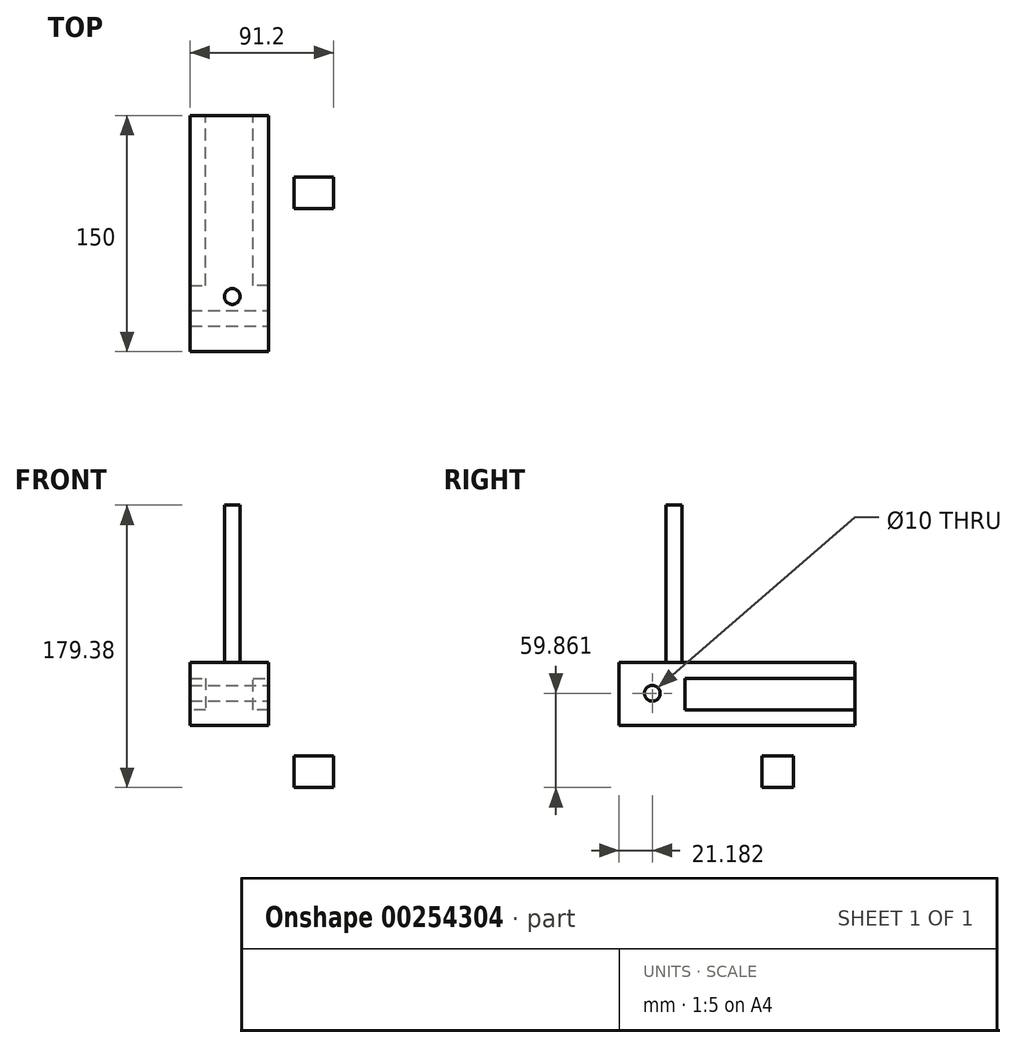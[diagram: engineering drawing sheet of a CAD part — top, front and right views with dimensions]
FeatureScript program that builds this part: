
annotation { "Feature Type Name" : "Feature", "Feature Type Description" : "" }
export const myFeature = defineFeature(function(context is Context, id is Id, definition is map)
    precondition{}
    {
        {
            var Q0;
            Q0=qCreatedBy(makeId("Front.planeOp"),FACE);
            var sketch = newSketch(context, id + "F0", { "sketchPlane" : qUnion([Q0])});
            skLineSegment(sketch, "E0", {"start": v(-66.2, 25.63) * mm, "end": v(-16.2, 25.63) * mm});
            skLineSegment(sketch, "E1", {"start": v(-66.2, 25.63) * mm, "end": v(-66.2, 15.63) * mm});
            skLineSegment(sketch, "E2", {"start": v(-66.2, 15.63) * mm, "end": v(-56.2, 15.63) * mm});
            skLineSegment(sketch, "E3", {"start": v(-56.2, 15.63) * mm, "end": v(-56.2, -4.37) * mm});
            skLineSegment(sketch, "E4", {"start": v(-56.2, -4.37) * mm, "end": v(-66.2, -4.37) * mm});
            skLineSegment(sketch, "E5", {"start": v(-66.2, -4.37) * mm, "end": v(-66.2, -14.37) * mm});
            skLineSegment(sketch, "E6", {"start": v(-66.2, -14.37) * mm, "end": v(-16.2, -14.37) * mm});
            skLineSegment(sketch, "E7", {"start": v(-16.2, -14.37) * mm, "end": v(-16.2, -4.37) * mm});
            skLineSegment(sketch, "E8", {"start": v(-16.2, -4.37) * mm, "end": v(-26.2, -4.37) * mm});
            skLineSegment(sketch, "E9", {"start": v(-26.2, -4.37) * mm, "end": v(-26.2, 15.63) * mm});
            skLineSegment(sketch, "E10", {"start": v(-26.2, 15.63) * mm, "end": v(-16.2, 15.63) * mm});
            skLineSegment(sketch, "E11", {"start": v(-16.2, 15.63) * mm, "end": v(-16.2, 25.63) * mm});
            skSolve(sketch);
        }
        {
            var Q0;
            Q0=makeQuery(id+"F0.imprint","IMPRINT",FACE,{"disambiguationData":[TD([[makeQuery(id+"F0.imprint","IMPRINT",EDGE,{"derivedFrom":sQuery(id+"F0.wireOp",EDGE,"E0")}),-1.0]])]});
            extrude(context, id + "F1", {"entities" : qUnion([Q0]), "depth" : 150 * mm});
        }
        {
            var Q0;
            Q0=qCreatedBy(makeId("Right.planeOp"),FACE);
            var sketch = newSketch(context, id + "F2", { "sketchPlane" : qUnion([Q0])});
            skLineSegment(sketch, "E12", {"start": v(-59.3, -33.75) * mm, "end": v(-39.3, -33.75) * mm});
            skLineSegment(sketch, "E13", {"start": v(-39.3, -33.75) * mm, "end": v(-39.3, -53.75) * mm});
            skLineSegment(sketch, "E14", {"start": v(-39.3, -53.75) * mm, "end": v(-59.3, -53.75) * mm});
            skLineSegment(sketch, "E15", {"start": v(-59.3, -53.75) * mm, "end": v(-59.3, -33.75) * mm});
            skSolve(sketch);
        }
        {
            var Q0;
            Q0=makeQuery(id+"F2.imprint","IMPRINT",FACE,{"disambiguationData":[TD([[makeQuery(id+"F2.imprint","IMPRINT",EDGE,{"derivedFrom":sQuery(id+"F2.wireOp",EDGE,"E12")}),-1.0]])]});
            extrude(context, id + "F3", {"entities" : qUnion([Q0]), "depth" : 25 * mm});
        }
        {
            var Q0;
            Q0=qCreatedBy(makeId("Right.planeOp"),FACE);
            var sketch = newSketch(context, id + "F4", { "sketchPlane" : qUnion([Q0])});
            skCircle(sketch, "E16", {"center": v(-49.4, -43.34) * mm, "radius": 5 * mm});
            skSolve(sketch);
        }
        {
            var Q0;
            Q0=makeQuery(id+"F4.imprint","IMPRINT",FACE,{"disambiguationData":[TD([[makeQuery(id+"F4.imprint","IMPRINT",EDGE,{"derivedFrom":sQuery(id+"F4.wireOp",EDGE,"E16")}),1.0]])]});
            extrude(context, id + "F5", {"entities" : qUnion([Q0]), "operationType" : NewBodyOperationType.ADD, "depth" : 15.2 * mm});
        }
        {
            var Q0;
            Q0=makeQuery(id+"F1.opExtrude","CAP_FACE",FACE,{"disambiguationData":[OSD([sQuery(id+"F0.wireOp",EDGE,"E0"),sQuery(id+"F0.wireOp",EDGE,"E1"),sQuery(id+"F0.wireOp",EDGE,"E2"),sQuery(id+"F0.wireOp",EDGE,"E3"),sQuery(id+"F0.wireOp",EDGE,"E4"),sQuery(id+"F0.wireOp",EDGE,"E5"),sQuery(id+"F0.wireOp",EDGE,"E6"),sQuery(id+"F0.wireOp",EDGE,"E7"),sQuery(id+"F0.wireOp",EDGE,"E8"),sQuery(id+"F0.wireOp",EDGE,"E9"),sQuery(id+"F0.wireOp",EDGE,"E10"),sQuery(id+"F0.wireOp",EDGE,"E11")])],"isStart":false});
            var sketch = newSketch(context, id + "F6", { "sketchPlane" : qUnion([Q0])});
            skLineSegment(sketch, "E17.bottom", {"start": v(-16.2, -14.37) * mm, "end": v(-66.2, -14.37) * mm});
            skLineSegment(sketch, "E17.top", {"start": v(-16.2, 25.63) * mm, "end": v(-66.2, 25.63) * mm});
            skLineSegment(sketch, "E17.left", {"start": v(-16.2, -14.37) * mm, "end": v(-16.2, 25.63) * mm});
            skLineSegment(sketch, "E17.right", {"start": v(-66.2, -14.37) * mm, "end": v(-66.2, 25.63) * mm});
            skSolve(sketch);
        }
        {
            var Q0;
            Q0 = qSketchRegion(id + "F6", true);
            extrude(context, id + "F7", {"entities" : qUnion([Q0]), "operationType" : NewBodyOperationType.ADD, "oppositeDirection" : true, "depth" : 42 * mm});
        }
        {
            var Q0;
            Q0=qCreatedBy(makeId("Right.planeOp"),FACE);
            var sketch = newSketch(context, id + "F8", { "sketchPlane" : qUnion([Q0])});
            skCircle(sketch, "E18", {"center": v(-128.82, 6.11) * mm, "radius": 5 * mm});
            skSolve(sketch);
        }
        {
            var Q0;
            Q0=makeQuery(id+"F8.imprint","IMPRINT",FACE,{"disambiguationData":[TD([[makeQuery(id+"F8.imprint","IMPRINT",EDGE,{"derivedFrom":sQuery(id+"F8.wireOp",EDGE,"E18")}),1.0]])]});
            extrude(context, id + "F9", {"entities" : qUnion([Q0]), "operationType" : NewBodyOperationType.REMOVE, "oppositeDirection" : true, "depth" : 74.4 * mm});
        }
        {
            var Q0;
            Q0=makeQuery(id+"F1.opExtrude","SWEPT_FACE",FACE,{"disambiguationData":[OSD([sQuery(id+"F0.wireOp",EDGE,"E0")])]});
            var sketch = newSketch(context, id + "F10", { "sketchPlane" : qUnion([Q0])});
            skCircle(sketch, "E19", {"center": v(-39.38, -115.03) * mm, "radius": 5 * mm});
            skSolve(sketch);
        }
        {
            var Q0;
            Q0=makeQuery(id+"F10.imprint","IMPRINT",FACE,{"disambiguationData":[TD([[makeQuery(id+"F10.imprint","IMPRINT",EDGE,{"derivedFrom":sQuery(id+"F10.wireOp",EDGE,"E19")}),1.0]])]});
            extrude(context, id + "F11", {"entities" : qUnion([Q0]), "depth" : 100 * mm});
        }
        {
            var Q0;
            Q0=sQuery(id+"F8.wireOp",EDGE,"E18");
            extrude(context, id + "F12", {"bodyType" : ToolBodyType.SURFACE, "surfaceEntities" : qUnion([Q0]), "oppositeDirection" : true, "depth" : 15 * mm});
        }
    });
